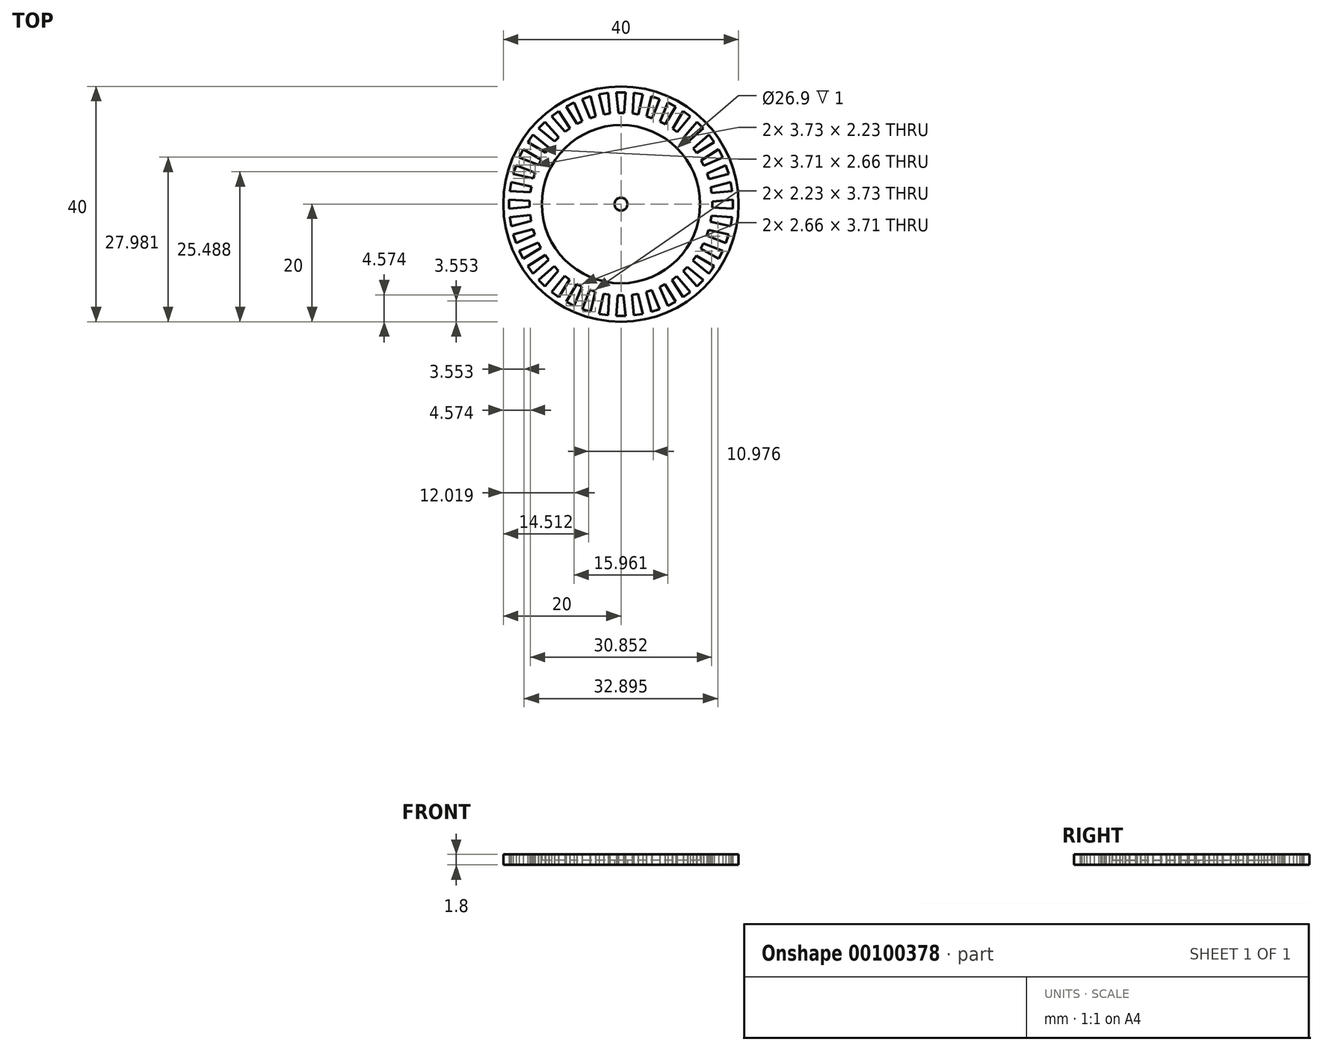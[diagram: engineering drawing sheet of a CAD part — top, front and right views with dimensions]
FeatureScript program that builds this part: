
annotation { "Feature Type Name" : "Feature", "Feature Type Description" : "" }
export const myFeature = defineFeature(function(context is Context, id is Id, definition is map)
    precondition{}
    {
        {
            var Q0;
            Q0=qCreatedBy(makeId("Top.planeOp"),FACE);
            var sketch = newSketch(context, id + "F0", { "sketchPlane" : qUnion([Q0])});
            skCircle(sketch, "E0", {"center": v(0, 0) * mm, "radius": 13.45 * mm});
            skCircle(sketch, "E1", {"center": v(0, 0) * mm, "radius": 20 * mm});
            skLineSegment(sketch, "E2", {"start": v(-19, 0.77) * mm, "end": v(-19, -0.77) * mm});
            skLineSegment(sketch, "E3", {"start": v(-15.51, 0.56) * mm, "end": v(-15.51, -0.44) * mm});
            skLineSegment(sketch, "E4", {"start": v(-19, 0.76) * mm, "end": v(-15.51, 0.56) * mm});
            skLineSegment(sketch, "E5", {"start": v(-15.51, -0.44) * mm, "end": v(-19, -0.77) * mm});
            skLineSegment(sketch, "E6.1.0", {"start": v(-18.9, -2.22) * mm, "end": v(-15.41, -1.87) * mm});
            skLineSegment(sketch, "E6.1.1", {"start": v(-15.25, -2.86) * mm, "end": v(-18.65, -3.73) * mm});
            skLineSegment(sketch, "E6.1.2", {"start": v(-15.41, -1.87) * mm, "end": v(-15.25, -2.86) * mm});
            skLineSegment(sketch, "E6.1.3", {"start": v(-18.9, -2.22) * mm, "end": v(-18.65, -3.73) * mm});
            skLineSegment(sketch, "E6.2.0", {"start": v(-18.31, -5.15) * mm, "end": v(-14.93, -4.26) * mm});
            skLineSegment(sketch, "E6.2.1", {"start": v(-14.62, -5.21) * mm, "end": v(-17.84, -6.6) * mm});
            skLineSegment(sketch, "E6.2.2", {"start": v(-14.93, -4.26) * mm, "end": v(-14.62, -5.21) * mm});
            skLineSegment(sketch, "E6.2.3", {"start": v(-18.31, -5.15) * mm, "end": v(-17.84, -6.6) * mm});
            skLineSegment(sketch, "E6.3.0", {"start": v(-17.28, -7.95) * mm, "end": v(-14.08, -6.54) * mm});
            skLineSegment(sketch, "E6.3.1", {"start": v(-13.62, -7.44) * mm, "end": v(-16.59, -9.31) * mm});
            skLineSegment(sketch, "E6.3.2", {"start": v(-14.08, -6.54) * mm, "end": v(-13.62, -7.44) * mm});
            skLineSegment(sketch, "E6.3.3", {"start": v(-17.28, -7.95) * mm, "end": v(-16.59, -9.31) * mm});
            skLineSegment(sketch, "E6.4.0", {"start": v(-15.83, -10.55) * mm, "end": v(-12.88, -8.67) * mm});
            skLineSegment(sketch, "E6.4.1", {"start": v(-12.3, -9.47) * mm, "end": v(-14.93, -11.8) * mm});
            skLineSegment(sketch, "E6.4.2", {"start": v(-12.88, -8.67) * mm, "end": v(-12.3, -9.47) * mm});
            skLineSegment(sketch, "E6.4.3", {"start": v(-15.83, -10.55) * mm, "end": v(-14.93, -11.8) * mm});
            skLineSegment(sketch, "E6.5.0", {"start": v(-13.98, -12.9) * mm, "end": v(-11.37, -10.57) * mm});
            skLineSegment(sketch, "E6.5.1", {"start": v(-10.66, -11.28) * mm, "end": v(-12.9, -13.98) * mm});
            skLineSegment(sketch, "E6.5.2", {"start": v(-11.37, -10.57) * mm, "end": v(-10.66, -11.28) * mm});
            skLineSegment(sketch, "E6.5.3", {"start": v(-13.98, -12.9) * mm, "end": v(-12.9, -13.98) * mm});
            skLineSegment(sketch, "E6.6.0", {"start": v(-11.8, -14.93) * mm, "end": v(-9.57, -12.22) * mm});
            skLineSegment(sketch, "E6.6.1", {"start": v(-8.76, -12.8) * mm, "end": v(-10.55, -15.83) * mm});
            skLineSegment(sketch, "E6.6.2", {"start": v(-9.57, -12.22) * mm, "end": v(-8.76, -12.8) * mm});
            skLineSegment(sketch, "E6.6.3", {"start": v(-11.8, -14.93) * mm, "end": v(-10.55, -15.83) * mm});
            skLineSegment(sketch, "E6.7.0", {"start": v(-9.31, -16.59) * mm, "end": v(-7.54, -13.57) * mm});
            skLineSegment(sketch, "E6.7.1", {"start": v(-6.65, -14.02) * mm, "end": v(-7.95, -17.28) * mm});
            skLineSegment(sketch, "E6.7.2", {"start": v(-7.54, -13.57) * mm, "end": v(-6.65, -14.02) * mm});
            skLineSegment(sketch, "E6.7.3", {"start": v(-9.31, -16.59) * mm, "end": v(-7.95, -17.28) * mm});
            skLineSegment(sketch, "E6.8.0", {"start": v(-6.6, -17.84) * mm, "end": v(-5.33, -14.58) * mm});
            skLineSegment(sketch, "E6.8.1", {"start": v(-4.38, -14.9) * mm, "end": v(-5.15, -18.31) * mm});
            skLineSegment(sketch, "E6.8.2", {"start": v(-5.33, -14.58) * mm, "end": v(-4.38, -14.9) * mm});
            skLineSegment(sketch, "E6.8.3", {"start": v(-6.6, -17.84) * mm, "end": v(-5.15, -18.31) * mm});
            skLineSegment(sketch, "E6.9.0", {"start": v(-3.73, -18.65) * mm, "end": v(-2.98, -15.23) * mm});
            skLineSegment(sketch, "E6.9.1", {"start": v(-2, -15.4) * mm, "end": v(-2.22, -18.9) * mm});
            skLineSegment(sketch, "E6.9.2", {"start": v(-2.98, -15.23) * mm, "end": v(-2, -15.4) * mm});
            skLineSegment(sketch, "E6.9.3", {"start": v(-3.73, -18.65) * mm, "end": v(-2.22, -18.9) * mm});
            skLineSegment(sketch, "E6.10.0", {"start": v(-0.77, -19) * mm, "end": v(-0.56, -15.51) * mm});
            skLineSegment(sketch, "E6.10.1", {"start": v(0.44, -15.51) * mm, "end": v(0.76, -19) * mm});
            skLineSegment(sketch, "E6.10.2", {"start": v(-0.56, -15.51) * mm, "end": v(0.44, -15.51) * mm});
            skLineSegment(sketch, "E6.10.3", {"start": v(-0.77, -19) * mm, "end": v(0.76, -19) * mm});
            skLineSegment(sketch, "E6.11.0", {"start": v(2.22, -18.9) * mm, "end": v(1.87, -15.41) * mm});
            skLineSegment(sketch, "E6.11.1", {"start": v(2.86, -15.25) * mm, "end": v(3.73, -18.65) * mm});
            skLineSegment(sketch, "E6.11.2", {"start": v(1.87, -15.41) * mm, "end": v(2.86, -15.25) * mm});
            skLineSegment(sketch, "E6.11.3", {"start": v(2.22, -18.9) * mm, "end": v(3.73, -18.65) * mm});
            skLineSegment(sketch, "E6.12.0", {"start": v(5.15, -18.31) * mm, "end": v(4.26, -14.93) * mm});
            skLineSegment(sketch, "E6.12.1", {"start": v(5.21, -14.62) * mm, "end": v(6.6, -17.84) * mm});
            skLineSegment(sketch, "E6.12.2", {"start": v(4.26, -14.93) * mm, "end": v(5.21, -14.62) * mm});
            skLineSegment(sketch, "E6.12.3", {"start": v(5.15, -18.31) * mm, "end": v(6.6, -17.84) * mm});
            skLineSegment(sketch, "E6.13.0", {"start": v(7.95, -17.28) * mm, "end": v(6.54, -14.08) * mm});
            skLineSegment(sketch, "E6.13.1", {"start": v(7.44, -13.62) * mm, "end": v(9.31, -16.59) * mm});
            skLineSegment(sketch, "E6.13.2", {"start": v(6.54, -14.08) * mm, "end": v(7.44, -13.62) * mm});
            skLineSegment(sketch, "E6.13.3", {"start": v(7.95, -17.28) * mm, "end": v(9.31, -16.59) * mm});
            skLineSegment(sketch, "E6.14.0", {"start": v(10.55, -15.83) * mm, "end": v(8.67, -12.88) * mm});
            skLineSegment(sketch, "E6.14.1", {"start": v(9.47, -12.3) * mm, "end": v(11.8, -14.93) * mm});
            skLineSegment(sketch, "E6.14.2", {"start": v(8.67, -12.88) * mm, "end": v(9.47, -12.3) * mm});
            skLineSegment(sketch, "E6.14.3", {"start": v(10.55, -15.83) * mm, "end": v(11.8, -14.93) * mm});
            skLineSegment(sketch, "E6.15.0", {"start": v(12.9, -13.98) * mm, "end": v(10.57, -11.37) * mm});
            skLineSegment(sketch, "E6.15.1", {"start": v(11.28, -10.66) * mm, "end": v(13.98, -12.9) * mm});
            skLineSegment(sketch, "E6.15.2", {"start": v(10.57, -11.37) * mm, "end": v(11.28, -10.66) * mm});
            skLineSegment(sketch, "E6.15.3", {"start": v(12.9, -13.98) * mm, "end": v(13.98, -12.9) * mm});
            skLineSegment(sketch, "E6.16.0", {"start": v(14.93, -11.8) * mm, "end": v(12.22, -9.57) * mm});
            skLineSegment(sketch, "E6.16.1", {"start": v(12.8, -8.76) * mm, "end": v(15.83, -10.55) * mm});
            skLineSegment(sketch, "E6.16.2", {"start": v(12.22, -9.57) * mm, "end": v(12.8, -8.76) * mm});
            skLineSegment(sketch, "E6.16.3", {"start": v(14.93, -11.8) * mm, "end": v(15.83, -10.55) * mm});
            skLineSegment(sketch, "E6.17.0", {"start": v(16.59, -9.31) * mm, "end": v(13.57, -7.54) * mm});
            skLineSegment(sketch, "E6.17.1", {"start": v(14.02, -6.65) * mm, "end": v(17.28, -7.95) * mm});
            skLineSegment(sketch, "E6.17.2", {"start": v(13.57, -7.54) * mm, "end": v(14.02, -6.65) * mm});
            skLineSegment(sketch, "E6.17.3", {"start": v(16.59, -9.31) * mm, "end": v(17.28, -7.95) * mm});
            skLineSegment(sketch, "E6.18.0", {"start": v(17.84, -6.6) * mm, "end": v(14.58, -5.33) * mm});
            skLineSegment(sketch, "E6.18.1", {"start": v(14.9, -4.38) * mm, "end": v(18.31, -5.15) * mm});
            skLineSegment(sketch, "E6.18.2", {"start": v(14.58, -5.33) * mm, "end": v(14.9, -4.38) * mm});
            skLineSegment(sketch, "E6.18.3", {"start": v(17.84, -6.6) * mm, "end": v(18.31, -5.15) * mm});
            skLineSegment(sketch, "E6.19.0", {"start": v(18.65, -3.73) * mm, "end": v(15.23, -2.98) * mm});
            skLineSegment(sketch, "E6.19.1", {"start": v(15.4, -2) * mm, "end": v(18.9, -2.22) * mm});
            skLineSegment(sketch, "E6.19.2", {"start": v(15.23, -2.98) * mm, "end": v(15.4, -2) * mm});
            skLineSegment(sketch, "E6.19.3", {"start": v(18.65, -3.73) * mm, "end": v(18.9, -2.22) * mm});
            skLineSegment(sketch, "E6.20.0", {"start": v(19, -0.77) * mm, "end": v(15.51, -0.56) * mm});
            skLineSegment(sketch, "E6.20.1", {"start": v(15.51, 0.44) * mm, "end": v(19, 0.76) * mm});
            skLineSegment(sketch, "E6.20.2", {"start": v(15.51, -0.56) * mm, "end": v(15.51, 0.44) * mm});
            skLineSegment(sketch, "E6.20.3", {"start": v(19, -0.77) * mm, "end": v(19, 0.76) * mm});
            skLineSegment(sketch, "E6.21.0", {"start": v(18.9, 2.22) * mm, "end": v(15.41, 1.87) * mm});
            skLineSegment(sketch, "E6.21.1", {"start": v(15.25, 2.86) * mm, "end": v(18.65, 3.73) * mm});
            skLineSegment(sketch, "E6.21.2", {"start": v(15.41, 1.87) * mm, "end": v(15.25, 2.86) * mm});
            skLineSegment(sketch, "E6.21.3", {"start": v(18.9, 2.22) * mm, "end": v(18.65, 3.73) * mm});
            skLineSegment(sketch, "E6.22.0", {"start": v(18.31, 5.15) * mm, "end": v(14.93, 4.26) * mm});
            skLineSegment(sketch, "E6.22.1", {"start": v(14.62, 5.21) * mm, "end": v(17.84, 6.6) * mm});
            skLineSegment(sketch, "E6.22.2", {"start": v(14.93, 4.26) * mm, "end": v(14.62, 5.21) * mm});
            skLineSegment(sketch, "E6.22.3", {"start": v(18.31, 5.15) * mm, "end": v(17.84, 6.6) * mm});
            skLineSegment(sketch, "E6.23.0", {"start": v(17.28, 7.95) * mm, "end": v(14.08, 6.54) * mm});
            skLineSegment(sketch, "E6.23.1", {"start": v(13.62, 7.44) * mm, "end": v(16.59, 9.31) * mm});
            skLineSegment(sketch, "E6.23.2", {"start": v(14.08, 6.54) * mm, "end": v(13.62, 7.44) * mm});
            skLineSegment(sketch, "E6.23.3", {"start": v(17.28, 7.95) * mm, "end": v(16.59, 9.31) * mm});
            skLineSegment(sketch, "E6.24.0", {"start": v(15.83, 10.55) * mm, "end": v(12.88, 8.67) * mm});
            skLineSegment(sketch, "E6.24.1", {"start": v(12.3, 9.47) * mm, "end": v(14.93, 11.8) * mm});
            skLineSegment(sketch, "E6.24.2", {"start": v(12.88, 8.67) * mm, "end": v(12.3, 9.47) * mm});
            skLineSegment(sketch, "E6.24.3", {"start": v(15.83, 10.55) * mm, "end": v(14.93, 11.8) * mm});
            skLineSegment(sketch, "E6.25.0", {"start": v(13.98, 12.9) * mm, "end": v(11.37, 10.57) * mm});
            skLineSegment(sketch, "E6.25.1", {"start": v(10.66, 11.28) * mm, "end": v(12.9, 13.98) * mm});
            skLineSegment(sketch, "E6.25.2", {"start": v(11.37, 10.57) * mm, "end": v(10.66, 11.28) * mm});
            skLineSegment(sketch, "E6.25.3", {"start": v(13.98, 12.9) * mm, "end": v(12.9, 13.98) * mm});
            skLineSegment(sketch, "E6.26.0", {"start": v(11.8, 14.93) * mm, "end": v(9.57, 12.22) * mm});
            skLineSegment(sketch, "E6.26.1", {"start": v(8.76, 12.8) * mm, "end": v(10.55, 15.83) * mm});
            skLineSegment(sketch, "E6.26.2", {"start": v(9.57, 12.22) * mm, "end": v(8.76, 12.8) * mm});
            skLineSegment(sketch, "E6.26.3", {"start": v(11.8, 14.93) * mm, "end": v(10.55, 15.83) * mm});
            skLineSegment(sketch, "E6.27.0", {"start": v(9.31, 16.59) * mm, "end": v(7.54, 13.57) * mm});
            skLineSegment(sketch, "E6.27.1", {"start": v(6.65, 14.02) * mm, "end": v(7.95, 17.28) * mm});
            skLineSegment(sketch, "E6.27.2", {"start": v(7.54, 13.57) * mm, "end": v(6.65, 14.02) * mm});
            skLineSegment(sketch, "E6.27.3", {"start": v(9.31, 16.59) * mm, "end": v(7.95, 17.28) * mm});
            skLineSegment(sketch, "E6.28.0", {"start": v(6.6, 17.84) * mm, "end": v(5.33, 14.58) * mm});
            skLineSegment(sketch, "E6.28.1", {"start": v(4.38, 14.9) * mm, "end": v(5.15, 18.31) * mm});
            skLineSegment(sketch, "E6.28.2", {"start": v(5.33, 14.58) * mm, "end": v(4.38, 14.9) * mm});
            skLineSegment(sketch, "E6.28.3", {"start": v(6.6, 17.84) * mm, "end": v(5.15, 18.31) * mm});
            skLineSegment(sketch, "E6.29.0", {"start": v(3.73, 18.65) * mm, "end": v(2.98, 15.23) * mm});
            skLineSegment(sketch, "E6.29.1", {"start": v(2, 15.4) * mm, "end": v(2.22, 18.9) * mm});
            skLineSegment(sketch, "E6.29.2", {"start": v(2.98, 15.23) * mm, "end": v(2, 15.4) * mm});
            skLineSegment(sketch, "E6.29.3", {"start": v(3.73, 18.65) * mm, "end": v(2.22, 18.9) * mm});
            skLineSegment(sketch, "E6.30.0", {"start": v(0.77, 19) * mm, "end": v(0.56, 15.51) * mm});
            skLineSegment(sketch, "E6.30.1", {"start": v(-0.44, 15.51) * mm, "end": v(-0.76, 19) * mm});
            skLineSegment(sketch, "E6.30.2", {"start": v(0.56, 15.51) * mm, "end": v(-0.44, 15.51) * mm});
            skLineSegment(sketch, "E6.30.3", {"start": v(0.77, 19) * mm, "end": v(-0.76, 19) * mm});
            skLineSegment(sketch, "E6.31.0", {"start": v(-2.22, 18.9) * mm, "end": v(-1.87, 15.41) * mm});
            skLineSegment(sketch, "E6.31.1", {"start": v(-2.86, 15.25) * mm, "end": v(-3.73, 18.65) * mm});
            skLineSegment(sketch, "E6.31.2", {"start": v(-1.87, 15.41) * mm, "end": v(-2.86, 15.25) * mm});
            skLineSegment(sketch, "E6.31.3", {"start": v(-2.22, 18.9) * mm, "end": v(-3.73, 18.65) * mm});
            skLineSegment(sketch, "E6.32.0", {"start": v(-5.15, 18.31) * mm, "end": v(-4.26, 14.93) * mm});
            skLineSegment(sketch, "E6.32.1", {"start": v(-5.21, 14.62) * mm, "end": v(-6.6, 17.84) * mm});
            skLineSegment(sketch, "E6.32.2", {"start": v(-4.26, 14.93) * mm, "end": v(-5.21, 14.62) * mm});
            skLineSegment(sketch, "E6.32.3", {"start": v(-5.15, 18.31) * mm, "end": v(-6.6, 17.84) * mm});
            skLineSegment(sketch, "E6.33.0", {"start": v(-7.95, 17.28) * mm, "end": v(-6.54, 14.08) * mm});
            skLineSegment(sketch, "E6.33.1", {"start": v(-7.44, 13.62) * mm, "end": v(-9.31, 16.59) * mm});
            skLineSegment(sketch, "E6.33.2", {"start": v(-6.54, 14.08) * mm, "end": v(-7.44, 13.62) * mm});
            skLineSegment(sketch, "E6.33.3", {"start": v(-7.95, 17.28) * mm, "end": v(-9.31, 16.59) * mm});
            skLineSegment(sketch, "E6.34.0", {"start": v(-10.55, 15.83) * mm, "end": v(-8.67, 12.88) * mm});
            skLineSegment(sketch, "E6.34.1", {"start": v(-9.47, 12.3) * mm, "end": v(-11.8, 14.93) * mm});
            skLineSegment(sketch, "E6.34.2", {"start": v(-8.67, 12.88) * mm, "end": v(-9.47, 12.3) * mm});
            skLineSegment(sketch, "E6.34.3", {"start": v(-10.55, 15.83) * mm, "end": v(-11.8, 14.93) * mm});
            skLineSegment(sketch, "E6.35.0", {"start": v(-12.9, 13.98) * mm, "end": v(-10.57, 11.37) * mm});
            skLineSegment(sketch, "E6.35.1", {"start": v(-11.28, 10.66) * mm, "end": v(-13.98, 12.9) * mm});
            skLineSegment(sketch, "E6.35.2", {"start": v(-10.57, 11.37) * mm, "end": v(-11.28, 10.66) * mm});
            skLineSegment(sketch, "E6.35.3", {"start": v(-12.9, 13.98) * mm, "end": v(-13.98, 12.9) * mm});
            skLineSegment(sketch, "E6.36.0", {"start": v(-14.93, 11.8) * mm, "end": v(-12.22, 9.57) * mm});
            skLineSegment(sketch, "E6.36.1", {"start": v(-12.8, 8.76) * mm, "end": v(-15.83, 10.55) * mm});
            skLineSegment(sketch, "E6.36.2", {"start": v(-12.22, 9.57) * mm, "end": v(-12.8, 8.76) * mm});
            skLineSegment(sketch, "E6.36.3", {"start": v(-14.93, 11.8) * mm, "end": v(-15.83, 10.55) * mm});
            skLineSegment(sketch, "E6.37.0", {"start": v(-16.59, 9.31) * mm, "end": v(-13.57, 7.54) * mm});
            skLineSegment(sketch, "E6.37.1", {"start": v(-14.02, 6.65) * mm, "end": v(-17.28, 7.95) * mm});
            skLineSegment(sketch, "E6.37.2", {"start": v(-13.57, 7.54) * mm, "end": v(-14.02, 6.65) * mm});
            skLineSegment(sketch, "E6.37.3", {"start": v(-16.59, 9.31) * mm, "end": v(-17.28, 7.95) * mm});
            skLineSegment(sketch, "E6.38.0", {"start": v(-17.84, 6.6) * mm, "end": v(-14.58, 5.33) * mm});
            skLineSegment(sketch, "E6.38.1", {"start": v(-14.9, 4.38) * mm, "end": v(-18.31, 5.15) * mm});
            skLineSegment(sketch, "E6.38.2", {"start": v(-14.58, 5.33) * mm, "end": v(-14.9, 4.38) * mm});
            skLineSegment(sketch, "E6.38.3", {"start": v(-17.84, 6.6) * mm, "end": v(-18.31, 5.15) * mm});
            skLineSegment(sketch, "E6.39.0", {"start": v(-18.65, 3.73) * mm, "end": v(-15.23, 2.98) * mm});
            skLineSegment(sketch, "E6.39.1", {"start": v(-15.4, 2) * mm, "end": v(-18.9, 2.22) * mm});
            skLineSegment(sketch, "E6.39.2", {"start": v(-15.23, 2.98) * mm, "end": v(-15.4, 2) * mm});
            skLineSegment(sketch, "E6.39.3", {"start": v(-18.65, 3.73) * mm, "end": v(-18.9, 2.22) * mm});
            skCircle(sketch, "E7", {"center": v(0, 0) * mm, "radius": 1.1 * mm});
            skSolve(sketch);
        }
        {
            var Q0;
            Q0=makeQuery(id+"F0.imprint","IMPRINT",FACE,{"disambiguationData":[TD([[makeQuery(id+"F0.imprint","IMPRINT",EDGE,{"derivedFrom":sQuery(id+"F0.wireOp",EDGE,"E0")}),-1.0]])]});
            extrude(context, id + "F1", {"entities" : qUnion([Q0]), "depth" : 1.8 * mm});
        }
        {
            var Q0;
            Q0=makeQuery(id+"F0.imprint","IMPRINT",FACE,{"disambiguationData":[TD([[makeQuery(id+"F0.imprint","IMPRINT",EDGE,{"derivedFrom":sQuery(id+"F0.wireOp",EDGE,"E0")}),1.0]])]});
            extrude(context, id + "F2", {"entities" : qUnion([Q0]), "operationType" : NewBodyOperationType.ADD, "depth" : 0.8 * mm});
        }
    });
